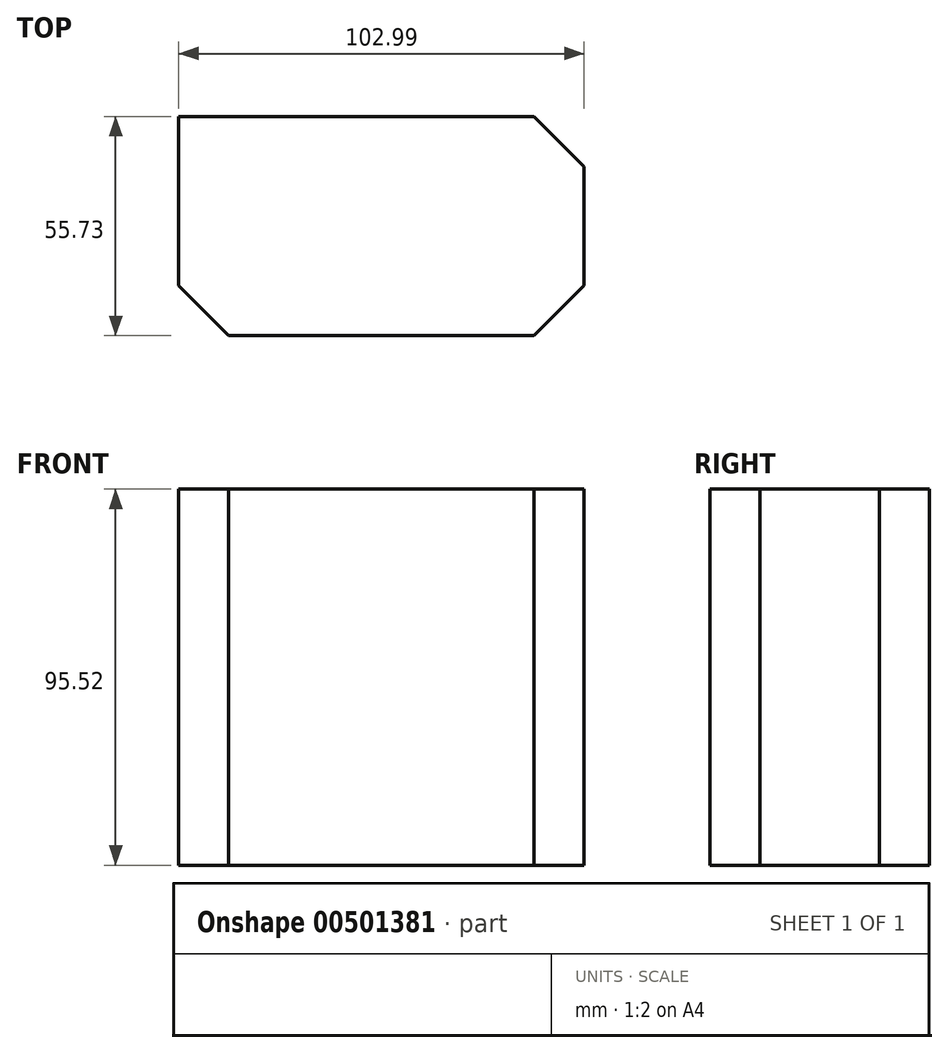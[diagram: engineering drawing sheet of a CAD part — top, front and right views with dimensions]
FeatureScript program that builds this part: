
annotation { "Feature Type Name" : "Feature", "Feature Type Description" : "" }
export const myFeature = defineFeature(function(context is Context, id is Id, definition is map)
    precondition{}
    {
        {
            var Q0;
            Q0=qCreatedBy(makeId("Top.planeOp"),FACE);
            var sketch = newSketch(context, id + "F0", { "sketchPlane" : qUnion([Q0])});
            skLineSegment(sketch, "E0.bottom", {"start": v(-55.85, -21.51) * mm, "end": v(47.14, -21.51) * mm});
            skLineSegment(sketch, "E0.top", {"start": v(-55.85, 34.22) * mm, "end": v(47.14, 34.22) * mm});
            skLineSegment(sketch, "E0.left", {"start": v(-55.85, -21.51) * mm, "end": v(-55.85, 34.22) * mm});
            skLineSegment(sketch, "E0.right", {"start": v(47.14, -21.51) * mm, "end": v(47.14, 34.22) * mm});
            skSolve(sketch);
        }
        {
            var Q0;
            Q0=makeQuery(id+"F0.imprint","IMPRINT",FACE,{"disambiguationData":[TD([[makeQuery(id+"F0.imprint","IMPRINT",EDGE,{"derivedFrom":sQuery(id+"F0.wireOp",EDGE,"E0.bottom")}),1.0]])]});
            extrude(context, id + "F1", {"entities" : qUnion([Q0]), "depth" : 95.52 * mm});
        }
        {
            var Q0;
            Q0=makeQuery(id+"F1.opExtrude","SWEPT_EDGE",EDGE,{"disambiguationData":[OSD([sQuery(id+"F0.wireOp",EDGE,"E0.bottom"),sQuery(id+"F0.wireOp",EDGE,"E0.right")])]});
            var Q1;
            Q1=makeQuery(id+"F1.opExtrude","SWEPT_EDGE",EDGE,{"disambiguationData":[OSD([sQuery(id+"F0.wireOp",EDGE,"E0.bottom"),sQuery(id+"F0.wireOp",EDGE,"E0.left")])]});
            var Q2;
            Q2=makeQuery(id+"F1.opExtrude","SWEPT_EDGE",EDGE,{"disambiguationData":[OSD([sQuery(id+"F0.wireOp",EDGE,"E0.top"),sQuery(id+"F0.wireOp",EDGE,"E0.right")])]});
            chamfer(context, id + "F2", {"entities" : qUnion([Q0, Q1, Q2]), "width" : 12.7 * mm, "tangentPropagation" : true});
        }
    });
